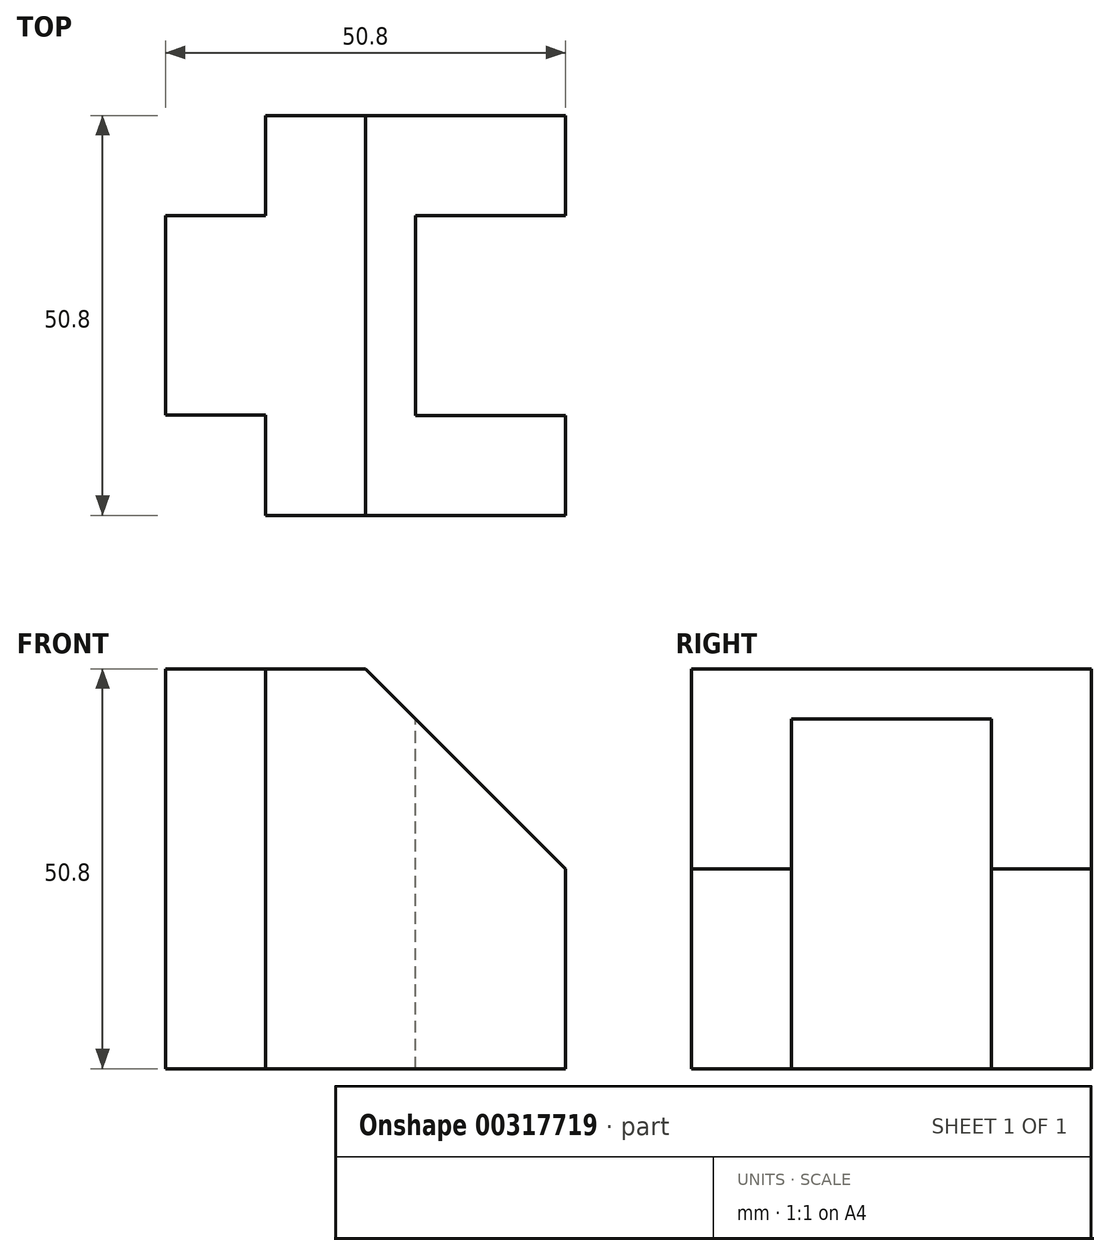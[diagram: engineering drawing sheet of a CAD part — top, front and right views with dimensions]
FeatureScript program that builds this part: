
annotation { "Feature Type Name" : "Feature", "Feature Type Description" : "" }
export const myFeature = defineFeature(function(context is Context, id is Id, definition is map)
    precondition{}
    {
        {
            var Q0;
            Q0=qCreatedBy(makeId("Front.planeOp"),FACE);
            var sketch = newSketch(context, id + "F0", { "sketchPlane" : qUnion([Q0])});
            skLineSegment(sketch, "E0", {"start": v(0, 0) * mm, "end": v(0, 50.8) * mm});
            skLineSegment(sketch, "E1", {"start": v(0, 50.8) * mm, "end": v(50.8, 50.8) * mm});
            skLineSegment(sketch, "E2", {"start": v(50.8, 50.8) * mm, "end": v(50.8, 0) * mm});
            skLineSegment(sketch, "E3", {"start": v(50.8, 0) * mm, "end": v(0, 0) * mm});
            skSolve(sketch);
        }
        {
            var Q0;
            Q0 = qSketchRegion(id + "F0", true);
            extrude(context, id + "F1", {"entities" : qUnion([Q0]), "depth" : 50.8 * mm});
        }
        {
            var Q0;
            Q0=makeQuery(id+"F1.opExtrude","CAP_FACE",FACE,{"disambiguationData":[OSD([sQuery(id+"F0.wireOp",EDGE,"E0"),sQuery(id+"F0.wireOp",EDGE,"E1"),sQuery(id+"F0.wireOp",EDGE,"E2"),sQuery(id+"F0.wireOp",EDGE,"E3")])],"isStart":false});
            var sketch = newSketch(context, id + "F2", { "sketchPlane" : qUnion([Q0])});
            skLineSegment(sketch, "E4", {"start": v(25.4, 50.8) * mm, "end": v(50.8, 25.4) * mm});
            skLineSegment(sketch, "E5", {"start": v(50.8, 25.4) * mm, "end": v(50.8, 50.8) * mm});
            skLineSegment(sketch, "E6", {"start": v(50.8, 50.8) * mm, "end": v(25.4, 50.8) * mm});
            skSolve(sketch);
        }
        {
            var Q0;
            Q0 = qSketchRegion(id + "F2", true);
            extrude(context, id + "F3", {"entities" : qUnion([Q0]), "operationType" : NewBodyOperationType.REMOVE, "endBound" : BoundingType.THROUGH_ALL, "oppositeDirection" : true, "depth" : 25.4 * mm});
        }
        {
            var Q0;
            Q0=makeQuery(id+"F1.opExtrude","SWEPT_FACE",FACE,{"disambiguationData":[OSD([sQuery(id+"F0.wireOp",EDGE,"E1")])]});
            var sketch = newSketch(context, id + "F4", { "sketchPlane" : qUnion([Q0])});
            skLineSegment(sketch, "E7", {"start": v(0, 0) * mm, "end": v(12.7, 0) * mm});
            skLineSegment(sketch, "E8", {"start": v(12.7, 0) * mm, "end": v(12.7, -12.7) * mm});
            skLineSegment(sketch, "E9", {"start": v(12.7, -12.7) * mm, "end": v(0, -12.7) * mm});
            skLineSegment(sketch, "E10", {"start": v(0, -12.7) * mm, "end": v(0, 0) * mm});
            skLineSegment(sketch, "E11", {"start": v(-18.4, -25.4) * mm, "end": v(67.69, -25.4) * mm, "construction": true});
            skPoint(sketch, "E11.startSnap0", {"position": v(0, -25.4) * mm});
            skPoint(sketch, "E11.endSnap0", {"position": v(25.4, -25.4) * mm});
            skLineSegment(sketch, "E12.MirrorCS", {"start": v(12.7, -38.1) * mm, "end": v(0, -38.1) * mm});
            skLineSegment(sketch, "E13.MirrorCS", {"start": v(0, -38.1) * mm, "end": v(0, -50.8) * mm});
            skLineSegment(sketch, "E14.MirrorCS", {"start": v(0, -50.8) * mm, "end": v(12.7, -50.8) * mm});
            skLineSegment(sketch, "E15.MirrorCS", {"start": v(12.7, -50.8) * mm, "end": v(12.7, -38.1) * mm});
            skSolve(sketch);
        }
        {
            var Q0;
            Q0 = qSketchRegion(id + "F4", true);
            extrude(context, id + "F5", {"entities" : qUnion([Q0]), "operationType" : NewBodyOperationType.REMOVE, "endBound" : BoundingType.THROUGH_ALL, "oppositeDirection" : true, "depth" : 25.4 * mm});
        }
        {
            var Q0;
            Q0=makeQuery(id+"F1.opExtrude","SWEPT_FACE",FACE,{"disambiguationData":[OSD([sQuery(id+"F0.wireOp",EDGE,"E1")])]});
            cPlane(context, id + "F6", {"entities" : qUnion([Q0]), "cplaneType" : CPlaneType.OFFSET, "offset" : 25.4 * mm, "width" : 152.4 * mm, "height" : 152.4 * mm});
        }
        {
            var Q0;
            Q0=qCreatedBy(id+"F6.planeOp",FACE);
            var sketch = newSketch(context, id + "F7", { "sketchPlane" : qUnion([Q0])});
            skLineSegment(sketch, "E16", {"start": v(50.8, -12.7) * mm, "end": v(31.75, -12.7) * mm});
            skLineSegment(sketch, "E17", {"start": v(31.75, -12.7) * mm, "end": v(31.75, -38.1) * mm});
            skLineSegment(sketch, "E18", {"start": v(31.75, -38.1) * mm, "end": v(50.8, -38.1) * mm});
            skLineSegment(sketch, "E19", {"start": v(50.8, -38.1) * mm, "end": v(50.8, -12.7) * mm});
            skSolve(sketch);
        }
        {
            var Q0;
            Q0 = qSketchRegion(id + "F7", true);
            extrude(context, id + "F8", {"entities" : qUnion([Q0]), "operationType" : NewBodyOperationType.REMOVE, "endBound" : BoundingType.THROUGH_ALL, "oppositeDirection" : true, "depth" : 25.4 * mm});
        }
    });
